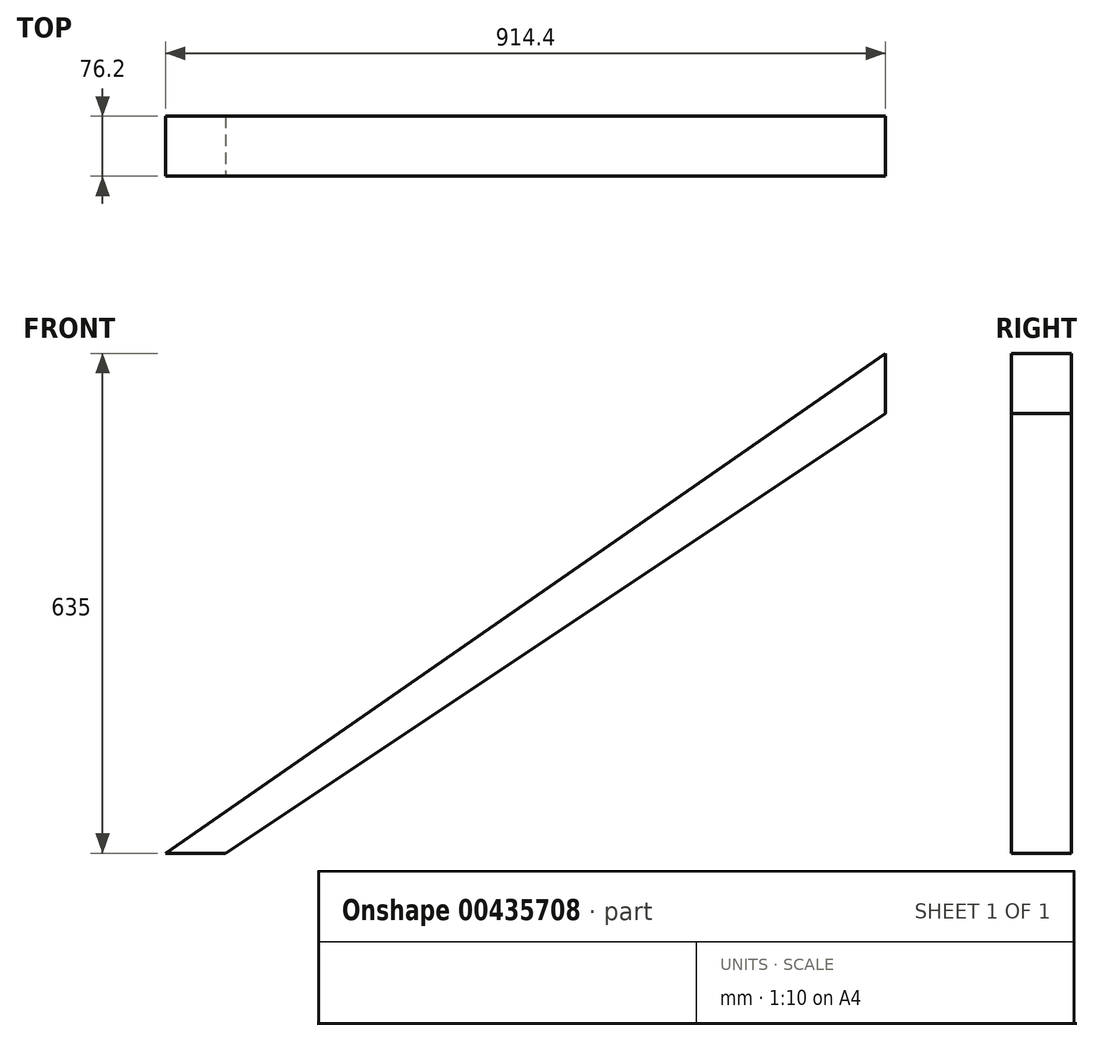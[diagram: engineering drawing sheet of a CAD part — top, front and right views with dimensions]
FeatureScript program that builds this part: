
annotation { "Feature Type Name" : "Feature", "Feature Type Description" : "" }
export const myFeature = defineFeature(function(context is Context, id is Id, definition is map)
    precondition{}
    {
        {
            var Q0;
            Q0=qCreatedBy(makeId("Front.planeOp"),FACE);
            var sketch = newSketch(context, id + "F0", { "sketchPlane" : qUnion([Q0])});
            skLineSegment(sketch, "E0", {"start": v(0, 0) * mm, "end": v(914.4, 0) * mm});
            skLineSegment(sketch, "E1", {"start": v(914.4, 0) * mm, "end": v(914.4, 635) * mm});
            skLineSegment(sketch, "E2", {"start": v(914.4, 635) * mm, "end": v(0, 0) * mm});
            skSolve(sketch);
        }
        {
            var Q0;
            Q0=makeQuery(id+"F0.imprint","IMPRINT",FACE,{"disambiguationData":[TD([[makeQuery(id+"F0.imprint","IMPRINT",EDGE,{"derivedFrom":sQuery(id+"F0.wireOp",EDGE,"E0")}),1.0]])]});
            extrude(context, id + "F1", {"entities" : qUnion([Q0]), "depth" : 76.2 * mm});
        }
        {
            var Q0;
            Q0=makeQuery(id+"F1.opExtrude","CAP_FACE",FACE,{"disambiguationData":[OSD([sQuery(id+"F0.wireOp",EDGE,"E0"),sQuery(id+"F0.wireOp",EDGE,"E1"),sQuery(id+"F0.wireOp",EDGE,"E2")])],"isStart":false});
            var sketch = newSketch(context, id + "F2", { "sketchPlane" : qUnion([Q0])});
            skLineSegment(sketch, "E3", {"start": v(914.4, 0) * mm, "end": v(914.4, 558.8) * mm});
            skLineSegment(sketch, "E4", {"start": v(914.4, 0) * mm, "end": v(76.2, 0) * mm});
            skLineSegment(sketch, "E5", {"start": v(76.2, 0) * mm, "end": v(914.4, 558.8) * mm});
            skSolve(sketch);
        }
        {
            var Q0;
            Q0=makeQuery(id+"F2.imprint","IMPRINT",FACE,{"disambiguationData":[TD([[makeQuery(id+"F2.imprint","IMPRINT",EDGE,{"derivedFrom":sQuery(id+"F2.wireOp",EDGE,"E3")}),1.0]])]});
            extrude(context, id + "F3", {"entities" : qUnion([Q0]), "operationType" : NewBodyOperationType.REMOVE, "oppositeDirection" : true, "depth" : 127 * mm});
        }
    });
